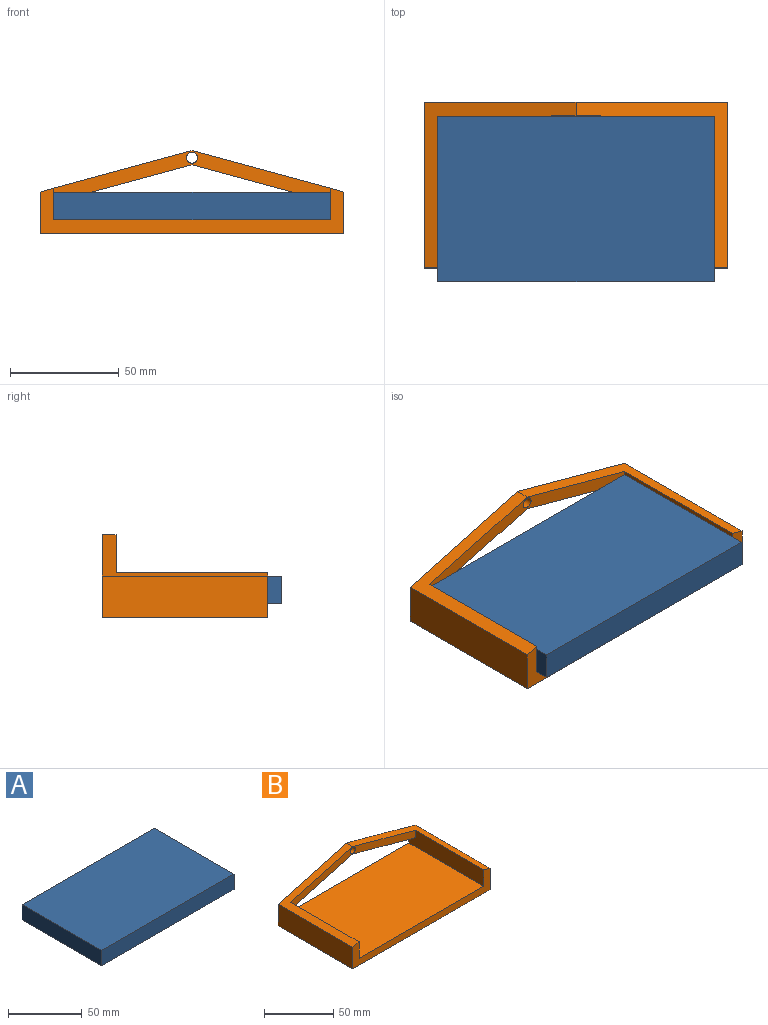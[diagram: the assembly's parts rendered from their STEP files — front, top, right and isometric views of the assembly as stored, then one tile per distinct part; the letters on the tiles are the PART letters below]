
ASSEMBLY  parts=2 mates=1
PART A: 6 faces, bbox 127x76.2x12.7 mm
  f0: plane 127x12.7mm, normal (0,-1,0), area 1612.9mm2, adj f1,f3,f4,f5
  f1: plane 76.2x12.7mm, normal (1,0,0), area 967.7mm2, adj f0,f2,f4,f5
  f2: plane 127x12.7mm, normal (0,1,0), area 1612.9mm2, adj f1,f3,f4,f5
  f3: plane 76.2x12.7mm, normal (-1,0,0), area 967.7mm2, adj f0,f2,f4,f5
  f4: plane 127x76.2mm, normal (0,0,1), area 9677.4mm2, adj f0,f1,f2,f3
  f5: plane 127x76.2mm, normal (0,0,-1), area 9677.4mm2, adj f0,f1,f2,f3
PART B: 14 faces, bbox 139.7x76.2x38.1 mm
  f0: plane 139.7x76.2mm, normal (0,0,-1), area 10645.1mm2, adj f3,f4,f5,f9
  f1: plane 76.2x69.85mm, normal (-0.26,0,0.96), area 919.5mm2, adj f2,f3,f5,f6,f9,f13
  f2: plane 76.2x69.85mm, normal (0.26,0,0.96), area 919.5mm2, adj f1,f3,f4,f7,f9,f13
  f3: plane 139.7x20.78mm, normal (0,-1,0), area 1059.4mm2, adj f0,f1,f2,f4,f5,f6,f7,f8
  f4: plane 76.2x19.05mm, normal (1,0,0), area 1451.6mm2, adj f0,f2,f3,f9
  f5: plane 76.2x19.05mm, normal (-1,0,0), area 1451.6mm2, adj f0,f1,f3,f9
  f6: plane 76.2x14.43mm, normal (1,0,0), area 1057.9mm2, adj f1,f3,f8,f9,f10,f13
  f7: plane 76.2x14.43mm, normal (-1,0,0), area 1057.9mm2, adj f2,f3,f8,f9,f11,f13
  f8: plane 127x76.2mm, normal (0,0,1), area 9677.4mm2, adj f3,f6,f7,f9
  f9: plane 139.7x38.1mm, normal (0,1,0), area 1875mm2, adj f0,f1,f2,f4,f5,f6,f7,f8
  f10: plane 63.5x17.32mm, normal (0.26,0,-0.96), area 418mm2, adj f6,f9,f11,f13
  f11: plane 63.5x17.32mm, normal (-0.26,0,-0.96), area 418mm2, adj f7,f9,f10,f13
  f12: cylinder r=2.54mm len=6.35mm, axis (0,1,0), area 101.3mm2, adj f9,f13
  f13: plane 127x23.9mm, normal (0,-1,0), area 815.6mm2, adj f1,f2,f6,f7,f10,f11,f12
PLACE A t=(0,-9.53,-3.18)mm
PLACE B at identity
MATE planar A.f5 <-> B.f8  axis (0,0,-1) through (0,28.57,-3.17)mm
